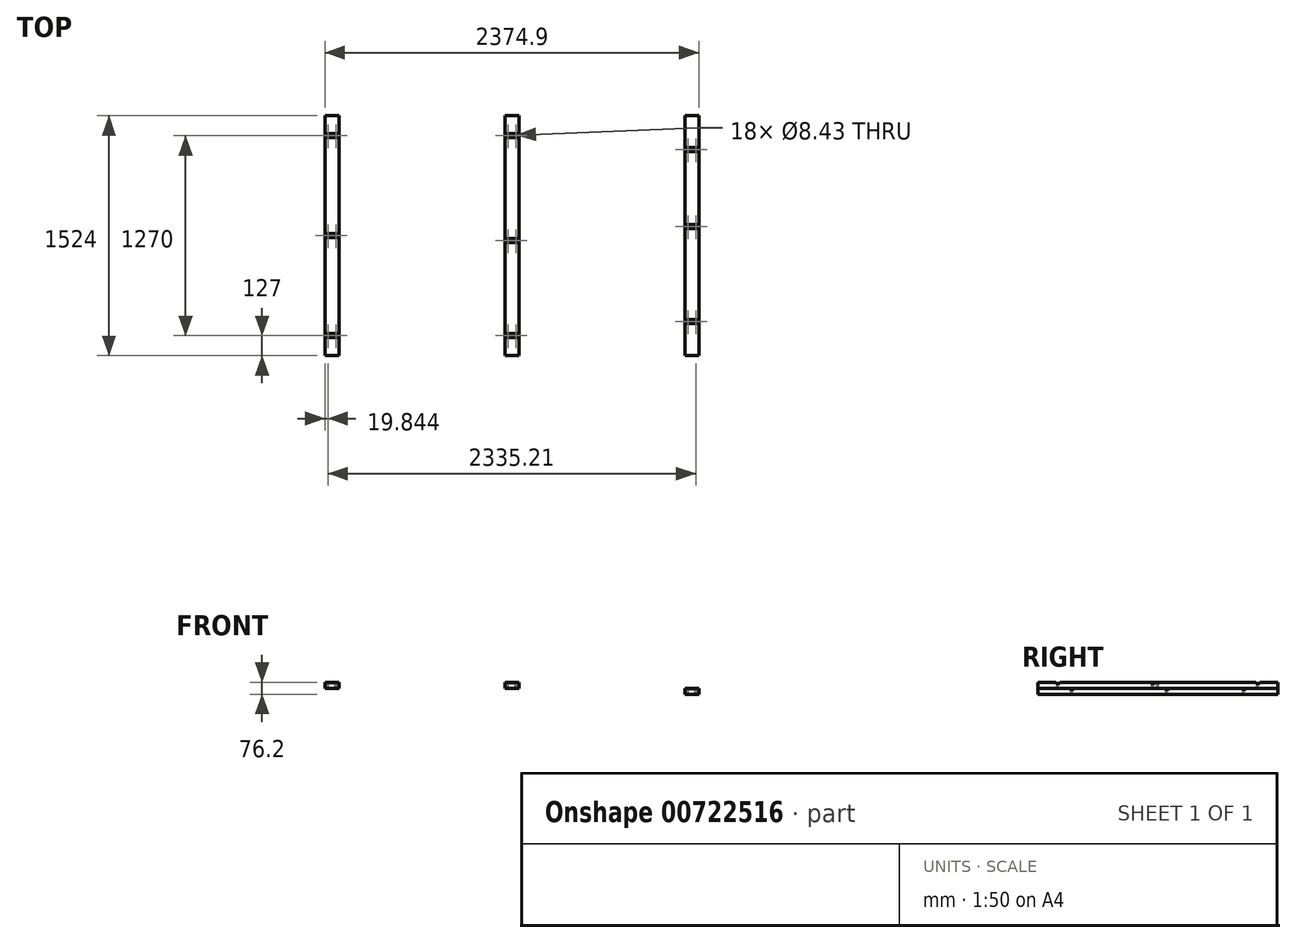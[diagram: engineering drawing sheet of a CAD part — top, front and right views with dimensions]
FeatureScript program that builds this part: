
annotation { "Feature Type Name" : "Feature", "Feature Type Description" : "" }
export const myFeature = defineFeature(function(context is Context, id is Id, definition is map)
    precondition{}
    {
        {
            var Q0;
            Q0=qCreatedBy(makeId("Front.planeOp"),FACE);
            var sketch = newSketch(context, id + "F0", { "sketchPlane" : qUnion([Q0])});
            skLineSegment(sketch, "E0.bottom", {"start": v(-44.45, 19.05) * mm, "end": v(44.45, 19.05) * mm});
            skLineSegment(sketch, "E0.top", {"start": v(-44.45, -19.05) * mm, "end": v(44.45, -19.05) * mm});
            skLineSegment(sketch, "E0.left", {"start": v(-44.45, 19.05) * mm, "end": v(-44.45, -19.05) * mm});
            skLineSegment(sketch, "E0.right", {"start": v(44.45, 19.05) * mm, "end": v(44.45, -19.05) * mm});
            skLineSegment(sketch, "E1", {"start": v(-44.45, 19.05) * mm, "end": v(44.45, -19.05) * mm, "construction": true});
            skSolve(sketch);
        }
        {
            var Q0;
            Q0=qSketchRegion(id+"F0",true);
            extrude(context, id + "F1", {"entities" : qUnion([Q0]), "endBound" : BoundingType.SYMMETRIC, "depth" : 1524 * mm, "offsetDistance" : 25.4 * mm});
        }
        {
            var Q0;
            Q0=makeQuery(id+"F1.opExtrude","SWEPT_FACE",FACE,{"disambiguationData":[OSD([sQuery(id+"F0.wireOp",EDGE,"E0.bottom")])]});
            var sketch = newSketch(context, id + "F2", { "sketchPlane" : qUnion([Q0])});
            skLineSegment(sketch, "E2.bottom", {"start": v(-44.45, 647.7) * mm, "end": v(44.45, 647.7) * mm});
            skLineSegment(sketch, "E2.top", {"start": v(-44.45, 622.3) * mm, "end": v(44.45, 622.3) * mm});
            skLineSegment(sketch, "E2.left", {"start": v(-44.45, 647.7) * mm, "end": v(-44.45, 622.3) * mm});
            skLineSegment(sketch, "E2.right", {"start": v(44.45, 647.7) * mm, "end": v(44.45, 622.3) * mm});
            skLineSegment(sketch, "E3.bottom", {"start": v(-44.45, 762) * mm, "end": v(44.45, 762) * mm, "construction": true});
            skLineSegment(sketch, "E3.top", {"start": v(-44.45, 723.9) * mm, "end": v(44.45, 723.9) * mm, "construction": true});
            skLineSegment(sketch, "E3.left", {"start": v(-44.45, 762) * mm, "end": v(-44.45, 723.9) * mm, "construction": true});
            skLineSegment(sketch, "E3.right", {"start": v(44.45, 762) * mm, "end": v(44.45, 723.9) * mm, "construction": true});
            skLineSegment(sketch, "E4.MirrorCS", {"start": v(44.45, -647.7) * mm, "end": v(44.45, -622.3) * mm});
            skLineSegment(sketch, "E5.MirrorCS", {"start": v(-44.45, -647.7) * mm, "end": v(-44.45, -622.3) * mm});
            skLineSegment(sketch, "E6.MirrorCS", {"start": v(44.45, -762) * mm, "end": v(44.45, -723.9) * mm, "construction": true});
            skLineSegment(sketch, "E7.MirrorCS", {"start": v(-44.45, -762) * mm, "end": v(-44.45, -723.9) * mm, "construction": true});
            skLineSegment(sketch, "E8.MirrorCS", {"start": v(-44.45, -723.9) * mm, "end": v(44.45, -723.9) * mm, "construction": true});
            skLineSegment(sketch, "E9.MirrorCS", {"start": v(-44.45, -762) * mm, "end": v(44.45, -762) * mm, "construction": true});
            skLineSegment(sketch, "E10.MirrorCS", {"start": v(-44.45, -622.3) * mm, "end": v(44.45, -622.3) * mm});
            skLineSegment(sketch, "E11.MirrorCS", {"start": v(-44.45, -647.7) * mm, "end": v(44.45, -647.7) * mm});
            skLineSegment(sketch, "E12.bottom", {"start": v(-44.45, 12.7) * mm, "end": v(44.45, 12.7) * mm});
            skLineSegment(sketch, "E12.top", {"start": v(-44.45, -12.7) * mm, "end": v(44.45, -12.7) * mm});
            skLineSegment(sketch, "E12.left", {"start": v(-44.45, 12.7) * mm, "end": v(-44.45, -12.7) * mm});
            skLineSegment(sketch, "E12.right", {"start": v(44.45, 12.7) * mm, "end": v(44.45, -12.7) * mm});
            skLineSegment(sketch, "E13", {"start": v(-44.45, 12.7) * mm, "end": v(44.45, -12.7) * mm, "construction": true});
            skPoint(sketch, "E14", {"position": v(-24.6, 635) * mm});
            skLineSegment(sketch, "E15", {"start": v(0, 647.7) * mm, "end": v(0, 622.3) * mm, "construction": true});
            skLineSegment(sketch, "E16", {"start": v(-44.45, 635) * mm, "end": v(44.45, 635) * mm, "construction": true});
            skPoint(sketch, "E17.MirrorP", {"position": v(24.6, 635) * mm});
            skLineSegment(sketch, "E18", {"start": v(-44.45, 0) * mm, "end": v(44.45, 0) * mm, "construction": true});
            skPoint(sketch, "E19", {"position": v(-24.6, 0) * mm});
            skPoint(sketch, "E20.MirrorP", {"position": v(24.6, 0) * mm});
            skPoint(sketch, "E21.MirrorP", {"position": v(-24.6, -635) * mm});
            skPoint(sketch, "E22.MirrorP", {"position": v(24.6, -635) * mm});
            skSolve(sketch);
        }
        {
            var Q0;
            Q0=makeQuery(id+"F2.imprint","IMPRINT",FACE,{"disambiguationData":[TD([[makeQuery(id+"F2.imprint","IMPRINT",EDGE,{"derivedFrom":sQuery(id+"F2.wireOp",EDGE,"E2.bottom")}),-1.0]])]});
            var Q1;
            Q1=makeQuery(id+"F2.imprint","IMPRINT",FACE,{"disambiguationData":[TD([[makeQuery(id+"F2.imprint","IMPRINT",EDGE,{"derivedFrom":sQuery(id+"F2.wireOp",EDGE,"E4.MirrorCS")}),1.0]])]});
            var Q2;
            Q2=makeQuery(id+"F2.imprint","IMPRINT",FACE,{"disambiguationData":[TD([[makeQuery(id+"F2.imprint","IMPRINT",EDGE,{"derivedFrom":sQuery(id+"F2.wireOp",EDGE,"E12.bottom")}),-1.0]])]});
            extrude(context, id + "F3", {"entities" : qUnion([Q0, Q1, Q2]), "operationType" : NewBodyOperationType.REMOVE, "oppositeDirection" : true, "depth" : 6.35 * mm, "offsetDistance" : 25.4 * mm});
        }
        {
            var Q0;
            Q0=sQuery(id+"F2.wireOp",VERTEX,"E14");
            var Q1;
            Q1=sQuery(id+"F2.wireOp",VERTEX,"E17.MirrorP");
            var Q2;
            Q2=sQuery(id+"F2.wireOp",VERTEX,"E19");
            var Q3;
            Q3=sQuery(id+"F2.wireOp",VERTEX,"E20.MirrorP");
            var Q4;
            Q4=sQuery(id+"F2.wireOp",VERTEX,"E21.MirrorP");
            var Q5;
            Q5=sQuery(id+"F2.wireOp",VERTEX,"E22.MirrorP");
            var Q6;
            Q6=makeQuery(id+"F1.opExtrude","SWEPT_BODY",BODY,{"disambiguationData":[OSD([sQuery(id+"F0.wireOp",EDGE,"E0.bottom"),sQuery(id+"F0.wireOp",EDGE,"E0.top"),sQuery(id+"F0.wireOp",EDGE,"E0.left"),sQuery(id+"F0.wireOp",EDGE,"E0.right")])]});
            hole(context, id + "F4", {"style" : HoleStyle.SIMPLE, "endStyle" : HoleEndStyle.THROUGH, "standardTappedOrClearance" : lookupTablePath({ "standard" : "ANSI", "fit" : "Normal (ASME)", "size" : "5/16", "type" : "Clearance" }), "standardBlindInLast" : lookupTablePath({ "fit" : "Free", "standard" : "ANSI", "size" : "5/16", "type" : "Clearance" }), "holeDiameter" : 8.43 * mm, "majorDiameter" : 6.35 * mm, "isTappedThrough" : true, "tappedDepth" : 12.7 * mm, "tapClearance" : 3, "locations" : qUnion([Q0, Q1, Q2, Q3, Q4, Q5]), "scope" : qUnion([Q6])});
        }
        {
            var Q0;
            Q0=makeQuery(id+"F1.opExtrude","SWEPT_BODY",BODY,{"disambiguationData":[OSD([sQuery(id+"F0.wireOp",EDGE,"E0.bottom"),sQuery(id+"F0.wireOp",EDGE,"E0.top"),sQuery(id+"F0.wireOp",EDGE,"E0.left"),sQuery(id+"F0.wireOp",EDGE,"E0.right")])]});
            transform(context, id + "F5", {"entities" : qUnion([Q0]), "transformType" : TransformType.TRANSLATION_3D, "dx" : 1143 * mm, "dy" : 0 * mm, "dz" : 0 * mm, "makeCopy" : true});
        }
        {
            var Q0;
            Q0=makeQuery(id+"F5.opPattern","COPY",FACE,{"derivedFrom":makeQuery(id+"F1.opExtrude","SWEPT_FACE",FACE,{"disambiguationData":[OSD([sQuery(id+"F0.wireOp",EDGE,"E0.top")])]}),"instanceName":"1"});
            var sketch = newSketch(context, id + "F6", { "sketchPlane" : qUnion([Q0])});
            skLineSegment(sketch, "E23.bottom", {"start": v(2241.55, -762) * mm, "end": v(2330.45, -762) * mm});
            skLineSegment(sketch, "E23.top", {"start": v(2241.55, 762) * mm, "end": v(2330.45, 762) * mm});
            skLineSegment(sketch, "E23.left", {"start": v(2241.55, -762) * mm, "end": v(2241.55, 762) * mm});
            skLineSegment(sketch, "E23.right", {"start": v(2330.45, -762) * mm, "end": v(2330.45, 762) * mm});
            skSolve(sketch);
        }
        {
            var Q0;
            Q0=makeQuery(id+"F6.imprint","IMPRINT",FACE,{"disambiguationData":[TD([[makeQuery(id+"F6.imprint","IMPRINT",EDGE,{"derivedFrom":sQuery(id+"F6.wireOp",EDGE,"E23.bottom")}),1.0]])]});
            extrude(context, id + "F7", {"entities" : qUnion([Q0]), "depth" : 38.1 * mm, "offsetDistance" : 25.4 * mm});
        }
        {
            var Q0;
            Q0=makeQuery(id+"F7.opExtrude","CAP_FACE",FACE,{"disambiguationData":[OSD([sQuery(id+"F6.wireOp",EDGE,"E23.bottom"),sQuery(id+"F6.wireOp",EDGE,"E23.top"),sQuery(id+"F6.wireOp",EDGE,"E23.left"),sQuery(id+"F6.wireOp",EDGE,"E23.right")])],"isStart":true});
            var sketch = newSketch(context, id + "F8", { "sketchPlane" : qUnion([Q0])});
            skLineSegment(sketch, "E24.bottom", {"start": v(2241.55, 622.3) * mm, "end": v(2330.45, 622.3) * mm, "construction": true});
            skLineSegment(sketch, "E24.top", {"start": v(2241.55, 584.2) * mm, "end": v(2330.45, 584.2) * mm, "construction": true});
            skLineSegment(sketch, "E24.left", {"start": v(2241.55, 622.3) * mm, "end": v(2241.55, 584.2) * mm, "construction": true});
            skLineSegment(sketch, "E24.right", {"start": v(2330.45, 622.3) * mm, "end": v(2330.45, 584.2) * mm, "construction": true});
            skLineSegment(sketch, "E25.bottom", {"start": v(2241.55, 558.8) * mm, "end": v(2330.45, 558.8) * mm});
            skLineSegment(sketch, "E25.top", {"start": v(2241.55, 533.4) * mm, "end": v(2330.45, 533.4) * mm});
            skLineSegment(sketch, "E25.left", {"start": v(2241.55, 558.8) * mm, "end": v(2241.55, 533.4) * mm});
            skLineSegment(sketch, "E25.right", {"start": v(2330.45, 558.8) * mm, "end": v(2330.45, 533.4) * mm});
            skLineSegment(sketch, "E26", {"start": v(2330.45, 546.1) * mm, "end": v(2241.55, 546.1) * mm, "construction": true});
            skLineSegment(sketch, "E27", {"start": v(2286, 558.8) * mm, "end": v(2286, 533.4) * mm, "construction": true});
            skPoint(sketch, "E28", {"position": v(2261.4, 546.1) * mm});
            skPoint(sketch, "E29.MirrorP", {"position": v(2310.6, 546.1) * mm});
            skLineSegment(sketch, "E30.MirrorCS", {"start": v(2330.45, -546.1) * mm, "end": v(2241.55, -546.1) * mm, "construction": true});
            skLineSegment(sketch, "E31.MirrorCS", {"start": v(2330.45, -558.8) * mm, "end": v(2330.45, -533.4) * mm});
            skLineSegment(sketch, "E32.MirrorCS", {"start": v(2241.55, -558.8) * mm, "end": v(2241.55, -533.4) * mm});
            skLineSegment(sketch, "E33.MirrorCS", {"start": v(2241.55, -533.4) * mm, "end": v(2330.45, -533.4) * mm});
            skLineSegment(sketch, "E34.MirrorCS", {"start": v(2241.55, -558.8) * mm, "end": v(2330.45, -558.8) * mm});
            skLineSegment(sketch, "E35.MirrorCS", {"start": v(2330.45, -622.3) * mm, "end": v(2330.45, -584.2) * mm, "construction": true});
            skLineSegment(sketch, "E36.MirrorCS", {"start": v(2286, -558.8) * mm, "end": v(2286, -533.4) * mm, "construction": true});
            skLineSegment(sketch, "E37.MirrorCS", {"start": v(2241.55, -622.3) * mm, "end": v(2241.55, -584.2) * mm, "construction": true});
            skLineSegment(sketch, "E38.MirrorCS", {"start": v(2241.55, -622.3) * mm, "end": v(2330.45, -622.3) * mm, "construction": true});
            skPoint(sketch, "E39.MirrorP", {"position": v(2310.6, -546.1) * mm});
            skLineSegment(sketch, "E40.MirrorCS", {"start": v(2241.55, -584.2) * mm, "end": v(2330.45, -584.2) * mm, "construction": true});
            skPoint(sketch, "E41.MirrorP", {"position": v(2261.4, -546.1) * mm});
            skLineSegment(sketch, "E42", {"start": v(2241.55, 0) * mm, "end": v(2330.45, 0) * mm, "construction": true});
            skLineSegment(sketch, "E43.top", {"start": v(2241.55, 19.05) * mm, "end": v(2330.45, 19.05) * mm, "construction": true});
            skLineSegment(sketch, "E43.left", {"start": v(2241.55, 0) * mm, "end": v(2241.55, 19.05) * mm, "construction": true});
            skLineSegment(sketch, "E43.right", {"start": v(2330.45, 0) * mm, "end": v(2330.45, 19.05) * mm, "construction": true});
            skLineSegment(sketch, "E44.MirrorCS", {"start": v(2241.55, 0) * mm, "end": v(2241.55, -19.05) * mm, "construction": true});
            skLineSegment(sketch, "E45.MirrorCS", {"start": v(2241.55, -19.05) * mm, "end": v(2330.45, -19.05) * mm, "construction": true});
            skLineSegment(sketch, "E46.MirrorCS", {"start": v(2330.45, 0) * mm, "end": v(2330.45, -19.05) * mm, "construction": true});
            skLineSegment(sketch, "E47.bottom", {"start": v(2241.55, 44.45) * mm, "end": v(2330.45, 44.45) * mm});
            skLineSegment(sketch, "E47.top", {"start": v(2241.55, 69.85) * mm, "end": v(2330.45, 69.85) * mm});
            skLineSegment(sketch, "E47.left", {"start": v(2241.55, 44.45) * mm, "end": v(2241.55, 69.85) * mm});
            skLineSegment(sketch, "E47.right", {"start": v(2330.45, 44.45) * mm, "end": v(2330.45, 69.85) * mm});
            skLineSegment(sketch, "E48", {"start": v(2241.55, 57.15) * mm, "end": v(2330.45, 57.15) * mm, "construction": true});
            skLineSegment(sketch, "E49", {"start": v(2286, 69.85) * mm, "end": v(2286, 44.45) * mm, "construction": true});
            skPoint(sketch, "E50", {"position": v(2261.4, 57.15) * mm});
            skPoint(sketch, "E51.MirrorP", {"position": v(2310.6, 57.15) * mm});
            skSolve(sketch);
        }
        {
            var Q0;
            Q0=makeQuery(id+"F8.imprint","IMPRINT",FACE,{"disambiguationData":[TD([[makeQuery(id+"F8.imprint","IMPRINT",EDGE,{"derivedFrom":sQuery(id+"F8.wireOp",EDGE,"E25.bottom")}),-1.0]])]});
            var Q1;
            Q1=makeQuery(id+"F8.imprint","IMPRINT",FACE,{"disambiguationData":[TD([[makeQuery(id+"F8.imprint","IMPRINT",EDGE,{"derivedFrom":sQuery(id+"F8.wireOp",EDGE,"E47.bottom")}),1.0]])]});
            var Q2;
            Q2=makeQuery(id+"F8.imprint","IMPRINT",FACE,{"disambiguationData":[TD([[makeQuery(id+"F8.imprint","IMPRINT",EDGE,{"derivedFrom":sQuery(id+"F8.wireOp",EDGE,"E31.MirrorCS")}),-1.0]])]});
            extrude(context, id + "F9", {"entities" : qUnion([Q0, Q1, Q2]), "operationType" : NewBodyOperationType.REMOVE, "oppositeDirection" : true, "depth" : 6.35 * mm, "offsetDistance" : 25.4 * mm});
        }
        {
            var Q0;
            Q0=sQuery(id+"F8.wireOp",VERTEX,"E41.MirrorP");
            var Q1;
            Q1=sQuery(id+"F8.wireOp",VERTEX,"E39.MirrorP");
            var Q2;
            Q2=sQuery(id+"F8.wireOp",VERTEX,"E50");
            var Q3;
            Q3=sQuery(id+"F8.wireOp",VERTEX,"E51.MirrorP");
            var Q4;
            Q4=sQuery(id+"F8.wireOp",VERTEX,"E28");
            var Q5;
            Q5=sQuery(id+"F8.wireOp",VERTEX,"E29.MirrorP");
            var Q6;
            Q6=makeQuery(id+"F7.opExtrude","SWEPT_BODY",BODY,{"disambiguationData":[OSD([sQuery(id+"F6.wireOp",EDGE,"E23.bottom"),sQuery(id+"F6.wireOp",EDGE,"E23.top"),sQuery(id+"F6.wireOp",EDGE,"E23.left"),sQuery(id+"F6.wireOp",EDGE,"E23.right")])]});
            hole(context, id + "F10", {"style" : HoleStyle.SIMPLE, "endStyle" : HoleEndStyle.THROUGH, "standardTappedOrClearance" : lookupTablePath({ "standard" : "ANSI", "fit" : "Normal (ASME)", "size" : "5/16", "type" : "Clearance" }), "standardBlindInLast" : lookupTablePath({ "fit" : "Free", "standard" : "ANSI", "size" : "5/16", "type" : "Clearance" }), "holeDiameter" : 8.43 * mm, "majorDiameter" : 6.35 * mm, "isTappedThrough" : true, "tappedDepth" : 12.7 * mm, "tapClearance" : 3, "locations" : qUnion([Q0, Q1, Q2, Q3, Q4, Q5]), "scope" : qUnion([Q6])});
        }
        {
            var Q0;
            Q0=makeQuery(id+"F5.opPattern","COPY",FACE,{"derivedFrom":makeQuery(id+"F3.boolean.opBoolean","SPLIT",FACE,{"disambiguationData":[TD([makeQuery(id+"F3.opExtrude","SWEPT_FACE",FACE,{"disambiguationData":[OSD([sQuery(id+"F2.wireOp",EDGE,"E2.top")])]})])],"derivedFrom":makeQuery(id+"F1.opExtrude","SWEPT_FACE",FACE,{"disambiguationData":[OSD([sQuery(id+"F0.wireOp",EDGE,"E0.bottom")])]})}),"instanceName":"1"});
            var sketch = newSketch(context, id + "F11", { "sketchPlane" : qUnion([Q0])});
            skLineSegment(sketch, "E52.0", {"start": v(1098.55, 12.7) * mm, "end": v(1187.45, 12.7) * mm});
            skLineSegment(sketch, "E53.0", {"start": v(1098.55, -12.7) * mm, "end": v(1187.45, -12.7) * mm});
            skLineSegment(sketch, "E54.0", {"start": v(1098.55, -12.7) * mm, "end": v(1098.55, 12.7) * mm});
            skLineSegment(sketch, "E55.0", {"start": v(1187.45, -12.7) * mm, "end": v(1187.45, 12.7) * mm});
            skSolve(sketch);
        }
        {
            var Q0;
            Q0=makeQuery(id+"F11.imprint","IMPRINT",FACE,{"disambiguationData":[TD([[makeQuery(id+"F11.imprint","IMPRINT",EDGE,{"derivedFrom":sQuery(id+"F11.wireOp",EDGE,"E52.0")}),-1.0]])]});
            var Q1;
            Q1=makeQuery(id+"F5.opPattern","COPY",FACE,{"derivedFrom":makeQuery(id+"F1.opExtrude","SWEPT_FACE",FACE,{"disambiguationData":[OSD([sQuery(id+"F0.wireOp",EDGE,"E0.top")])]}),"instanceName":"1"});
            extrude(context, id + "F12", {"entities" : qUnion([Q0]), "endBound" : BoundingType.UP_TO_SURFACE, "oppositeDirection" : true, "depth" : 25.4 * mm, "endBoundEntityFace" : qUnion([Q1]), "offsetDistance" : 25.4 * mm});
        }
        {
            var Q0;
            Q0=makeQuery(id+"F5.opPattern","COPY",BODY,{"derivedFrom":makeQuery(id+"F1.opExtrude","SWEPT_BODY",BODY,{"disambiguationData":[OSD([sQuery(id+"F0.wireOp",EDGE,"E0.bottom"),sQuery(id+"F0.wireOp",EDGE,"E0.top"),sQuery(id+"F0.wireOp",EDGE,"E0.left"),sQuery(id+"F0.wireOp",EDGE,"E0.right")])]}),"instanceName":"1"});
            var Q1;
            Q1=makeQuery(id+"F12.opExtrude","SWEPT_BODY",BODY,{"disambiguationData":[OSD([sQuery(id+"F11.wireOp",EDGE,"E52.0"),sQuery(id+"F11.wireOp",EDGE,"E53.0"),sQuery(id+"F11.wireOp",EDGE,"E54.0"),sQuery(id+"F11.wireOp",EDGE,"E55.0")])]});
            booleanBodies(context, id + "F13", {"operationType" : BooleanOperationType.UNION, "tools" : qUnion([Q0, Q1])});
        }
        {
            var Q0;
            {var subQ2=makeQuery(id+"F1.opExtrude","SWEPT_FACE",FACE,{"disambiguationData":[OSD([sQuery(id+"F0.wireOp",EDGE,"E0.bottom")])]});Q0=makeQuery(id+"F13.opBoolean","MERGE",FACE,{"derivedFrom":[makeQuery(id+"F5.opPattern","COPY",FACE,{"derivedFrom":makeQuery(id+"F3.boolean.opBoolean","SPLIT",FACE,{"disambiguationData":[TD([makeQuery(id+"F3.opExtrude","SWEPT_FACE",FACE,{"disambiguationData":[OSD([sQuery(id+"F2.wireOp",EDGE,"E2.top")])]})])],"derivedFrom":subQ2}),"instanceName":"1"}),makeQuery(id+"F5.opPattern","COPY",FACE,{"derivedFrom":makeQuery(id+"F3.boolean.opBoolean","SPLIT",FACE,{"disambiguationData":[TD([makeQuery(id+"F3.opExtrude","SWEPT_FACE",FACE,{"disambiguationData":[OSD([sQuery(id+"F2.wireOp",EDGE,"E10.MirrorCS")])]})])],"derivedFrom":subQ2}),"instanceName":"1"}),makeQuery(id+"F12.opExtrude","CAP_FACE",FACE,{"disambiguationData":[OSD([sQuery(id+"F11.wireOp",EDGE,"E52.0"),sQuery(id+"F11.wireOp",EDGE,"E53.0"),sQuery(id+"F11.wireOp",EDGE,"E54.0"),sQuery(id+"F11.wireOp",EDGE,"E55.0")])],"isStart":true})]});}
            var sketch = newSketch(context, id + "F14", { "sketchPlane" : qUnion([Q0])});
            skLineSegment(sketch, "E56.bottom", {"start": v(1098.55, 0) * mm, "end": v(1187.45, 0) * mm, "construction": true});
            skLineSegment(sketch, "E56.top", {"start": v(1098.55, 19.05) * mm, "end": v(1187.45, 19.05) * mm, "construction": true});
            skLineSegment(sketch, "E56.left", {"start": v(1098.55, 0) * mm, "end": v(1098.55, 19.05) * mm, "construction": true});
            skLineSegment(sketch, "E56.right", {"start": v(1187.45, 0) * mm, "end": v(1187.45, 19.05) * mm, "construction": true});
            skLineSegment(sketch, "E57.MirrorCS", {"start": v(1098.55, 0) * mm, "end": v(1098.55, -19.05) * mm, "construction": true});
            skLineSegment(sketch, "E58.MirrorCS", {"start": v(1187.45, 0) * mm, "end": v(1187.45, -19.05) * mm, "construction": true});
            skLineSegment(sketch, "E59.MirrorCS", {"start": v(1098.55, -19.05) * mm, "end": v(1187.45, -19.05) * mm, "construction": true});
            skLineSegment(sketch, "E60.bottom", {"start": v(1098.55, -19.05) * mm, "end": v(1187.45, -19.05) * mm});
            skLineSegment(sketch, "E60.top", {"start": v(1098.55, -44.45) * mm, "end": v(1187.45, -44.45) * mm});
            skLineSegment(sketch, "E60.left", {"start": v(1098.55, -19.05) * mm, "end": v(1098.55, -44.45) * mm});
            skLineSegment(sketch, "E60.right", {"start": v(1187.45, -19.05) * mm, "end": v(1187.45, -44.45) * mm});
            skLineSegment(sketch, "E61", {"start": v(1143, -19.05) * mm, "end": v(1143, -44.45) * mm, "construction": true});
            skLineSegment(sketch, "E62", {"start": v(1098.55, -31.75) * mm, "end": v(1187.45, -31.75) * mm, "construction": true});
            skPoint(sketch, "E63", {"position": v(1118.4, -31.75) * mm});
            skPoint(sketch, "E64.MirrorP", {"position": v(1167.6, -31.75) * mm});
            skSolve(sketch);
        }
        {
            var Q0;
            Q0=makeQuery(id+"F14.imprint","IMPRINT",FACE,{"disambiguationData":[TD([[makeQuery(id+"F14.imprint","IMPRINT",EDGE,{"derivedFrom":sQuery(id+"F14.wireOp",EDGE,"E60.bottom")}),-1.0]])]});
            extrude(context, id + "F15", {"entities" : qUnion([Q0]), "operationType" : NewBodyOperationType.REMOVE, "oppositeDirection" : true, "depth" : 6.35 * mm, "offsetDistance" : 25.4 * mm});
        }
        {
            var Q0;
            Q0=sQuery(id+"F14.wireOp",VERTEX,"E63");
            var Q1;
            Q1=sQuery(id+"F14.wireOp",VERTEX,"E64.MirrorP");
            var Q2;
            Q2=makeQuery(id+"F5.opPattern","COPY",BODY,{"derivedFrom":makeQuery(id+"F1.opExtrude","SWEPT_BODY",BODY,{"disambiguationData":[OSD([sQuery(id+"F0.wireOp",EDGE,"E0.bottom"),sQuery(id+"F0.wireOp",EDGE,"E0.top"),sQuery(id+"F0.wireOp",EDGE,"E0.left"),sQuery(id+"F0.wireOp",EDGE,"E0.right")])]}),"instanceName":"1"});
            hole(context, id + "F16", {"style" : HoleStyle.SIMPLE, "endStyle" : HoleEndStyle.THROUGH, "standardTappedOrClearance" : lookupTablePath({ "standard" : "ANSI", "fit" : "Normal (ASME)", "size" : "5/16", "type" : "Clearance" }), "standardBlindInLast" : lookupTablePath({ "fit" : "Free", "standard" : "ANSI", "size" : "5/16", "type" : "Clearance" }), "holeDiameter" : 8.43 * mm, "majorDiameter" : 6.35 * mm, "isTappedThrough" : true, "tappedDepth" : 12.7 * mm, "tapClearance" : 3, "locations" : qUnion([Q0, Q1]), "scope" : qUnion([Q2])});
        }
    });
